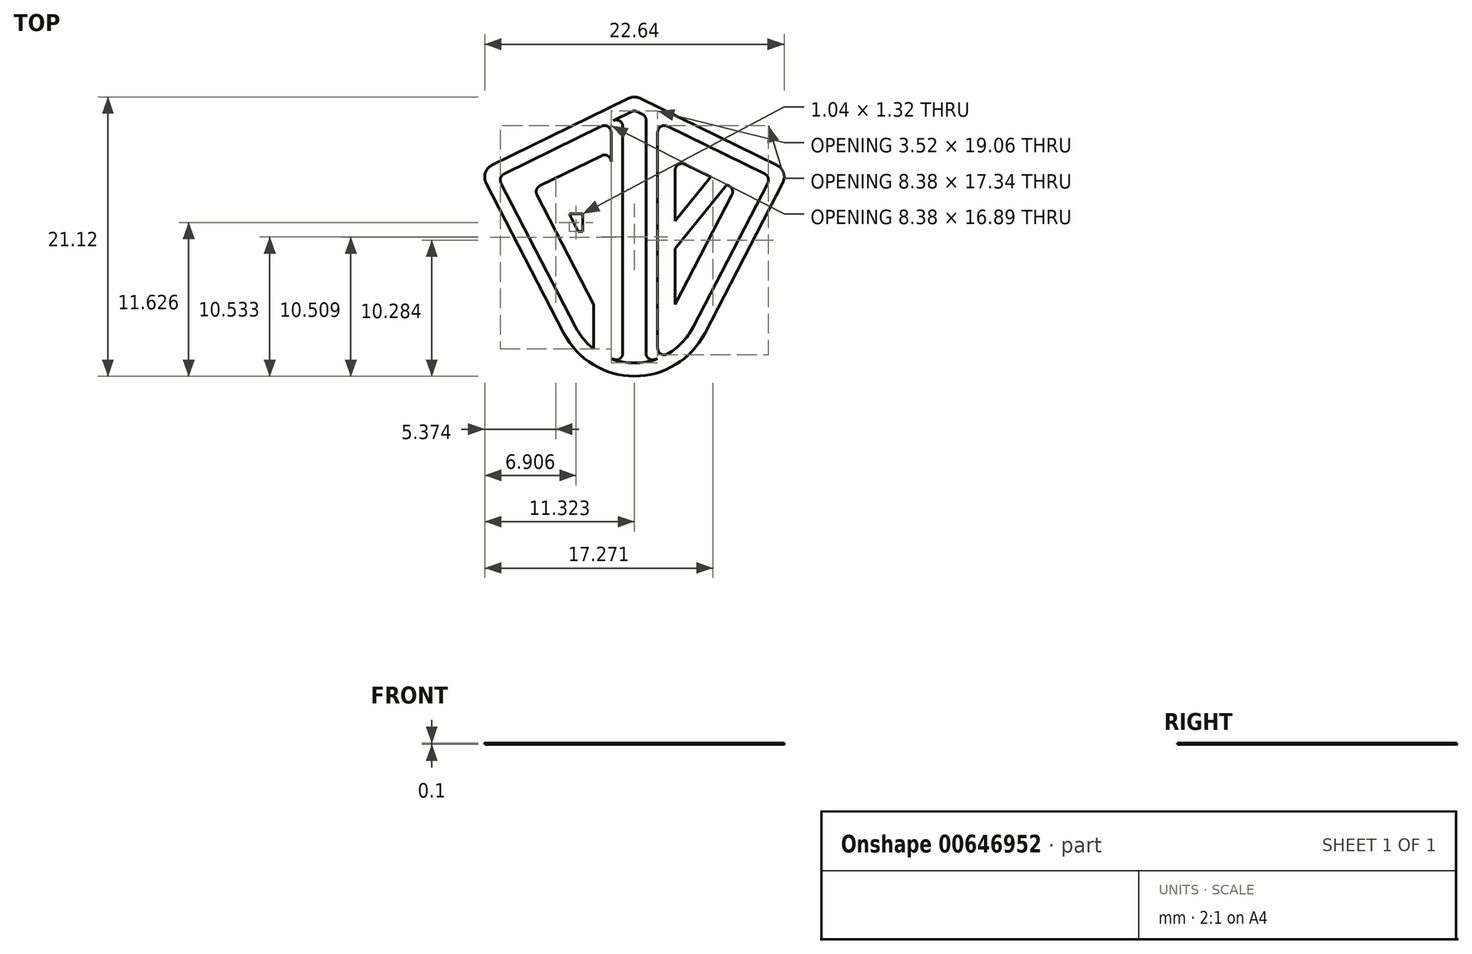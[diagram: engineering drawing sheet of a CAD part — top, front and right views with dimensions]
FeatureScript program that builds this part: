
annotation { "Feature Type Name" : "Feature", "Feature Type Description" : "" }
export const myFeature = defineFeature(function(context is Context, id is Id, definition is map)
    precondition{}
    {
        {
            var Q0;
            Q0=qCreatedBy(makeId("Top.planeOp"),FACE);
            var sketch = newSketch(context, id + "F0", { "sketchPlane" : qUnion([Q0])});
            skArc(sketch, "E0.MirrorCS", {"start": v(-12.62, 8.93) * mm, "mid": v(-12.18, 9.03) * mm, "end": v(-11.74, 8.93) * mm});
            skArc(sketch, "E1.MirrorCS", {"start": v(-1.42, 3.88) * mm, "mid": v(-0.9, 3.3) * mm, "end": v(-0.97, 2.52) * mm});
            skArc(sketch, "E2.MirrorCS", {"start": v(-23.38, 2.52) * mm, "mid": v(-23.45, 3.3) * mm, "end": v(-22.94, 3.88) * mm});
            skPoint(sketch, "E3.MirrorP", {"position": v(-23.85, 3.43) * mm});
            skArc(sketch, "E4.MirrorCS", {"start": v(-6.85, -8.84) * mm, "mid": v(-12.18, -12.09) * mm, "end": v(-17.5, -8.84) * mm});
            skLineSegment(sketch, "E5.MirrorCS", {"start": v(-6.85, -8.84) * mm, "end": v(-0.97, 2.52) * mm});
            skLineSegment(sketch, "E6.MirrorCS", {"start": v(-12.62, 8.93) * mm, "end": v(-22.94, 3.88) * mm});
            skLineSegment(sketch, "E7.MirrorCS", {"start": v(-23.38, 2.52) * mm, "end": v(-17.5, -8.84) * mm});
            skLineSegment(sketch, "E8.MirrorCS", {"start": v(-1.42, 3.88) * mm, "end": v(-11.74, 8.93) * mm});
            skLineSegment(sketch, "E9", {"start": v(-22.26, 2.53) * mm, "end": v(-16.62, -8.38) * mm});
            skArc(sketch, "E10.filletArc", {"start": v(-9.67, -10.41) * mm, "mid": v(-8.56, -9.53) * mm, "end": v(-7.74, -8.38) * mm});
            skLineSegment(sketch, "E11.MirrorCS", {"start": v(-10.42, 6.37) * mm, "end": v(-10.42, -9.98) * mm});
            skLineSegment(sketch, "E12.bottom", {"start": v(-15.25, 0.2) * mm, "end": v(-16.07, 0.2) * mm});
            skLineSegment(sketch, "E12.top", {"start": v(-15.75, -1.12) * mm, "end": v(-16.07, -1.12) * mm});
            skLineSegment(sketch, "E13", {"start": v(-15.25, 0.2) * mm, "end": v(-14.44, 0.2) * mm});
            skPoint(sketch, "E14", {"position": v(-16.57, -8.47) * mm});
            skPoint(sketch, "E15", {"position": v(-15.25, -10.03) * mm});
            skPoint(sketch, "E16", {"position": v(-13.94, -10.77) * mm});
            skPoint(sketch, "E17", {"position": v(-13.06, -11) * mm});
            skPoint(sketch, "E18", {"position": v(-11.3, -11) * mm});
            skPoint(sketch, "E19", {"position": v(-10.42, -10.77) * mm});
            skPoint(sketch, "E20", {"position": v(-9.1, -10.03) * mm});
            skPoint(sketch, "E21", {"position": v(-9.1, -6.67) * mm});
            skPoint(sketch, "E22", {"position": v(-2.78, 1.2) * mm});
            skPoint(sketch, "E23", {"position": v(-4.57, 2.08) * mm});
            skPoint(sketch, "E24", {"position": v(-9.1, 4.3) * mm});
            skPoint(sketch, "E25", {"position": v(-9.1, 6.52) * mm});
            skPoint(sketch, "E26", {"position": v(-10.42, 7.17) * mm});
            skPoint(sketch, "E27", {"position": v(-11.3, 7.6) * mm});
            skPoint(sketch, "E28", {"position": v(-13.06, 7.6) * mm});
            skPoint(sketch, "E29", {"position": v(-13.94, 7.17) * mm});
            skPoint(sketch, "E30", {"position": v(-15.25, 4.3) * mm});
            skPoint(sketch, "E31", {"position": v(-13.94, 4.94) * mm});
            skPoint(sketch, "E32", {"position": v(-13.06, 5.37) * mm});
            skPoint(sketch, "E33", {"position": v(-10.42, 4.94) * mm});
            skPoint(sketch, "E34", {"position": v(-11.3, 5.37) * mm});
            skPoint(sketch, "E35", {"position": v(-21.58, 1.2) * mm});
            skPoint(sketch, "E36", {"position": v(-19.78, 2.08) * mm});
            skPoint(sketch, "E37", {"position": v(-16.57, -4.12) * mm});
            skPoint(sketch, "E38", {"position": v(-16.57, -1.12) * mm});
            skPoint(sketch, "E39", {"position": v(-16.57, 0.2) * mm});
            skPoint(sketch, "E40", {"position": v(-15.25, 0.2) * mm});
            skPoint(sketch, "E41", {"position": v(-15.25, -1.12) * mm});
            skPoint(sketch, "E42", {"position": v(-13.94, 0.2) * mm});
            skLineSegment(sketch, "E43", {"start": v(-7.74, -8.38) * mm, "end": v(-2.78, 1.2) * mm});
            skLineSegment(sketch, "E44", {"start": v(-2.78, 1.2) * mm, "end": v(-2.1, 2.53) * mm});
            skLineSegment(sketch, "E45", {"start": v(-2.32, 3.2) * mm, "end": v(-9.1, 6.52) * mm});
            skLineSegment(sketch, "E46", {"start": v(-9.1, -6.67) * mm, "end": v(-4.8, 1.63) * mm});
            skLineSegment(sketch, "E47", {"start": v(-5.03, 2.3) * mm, "end": v(-8.38, 3.94) * mm});
            skLineSegment(sketch, "E48", {"start": v(-9.1, 3.5) * mm, "end": v(-9.1, -6.67) * mm});
            skLineSegment(sketch, "E49", {"start": v(-22.04, 3.2) * mm, "end": v(-14.65, 6.82) * mm});
            skLineSegment(sketch, "E50", {"start": v(-12.78, 7.74) * mm, "end": v(-12.4, 7.92) * mm});
            skLineSegment(sketch, "E51", {"start": v(-11.96, 7.92) * mm, "end": v(-11.58, 7.74) * mm});
            skLineSegment(sketch, "E52", {"start": v(-15.25, 4.3) * mm, "end": v(-19.32, 2.3) * mm});
            skLineSegment(sketch, "E53", {"start": v(-19.55, 1.63) * mm, "end": v(-16.57, -4.12) * mm});
            skLineSegment(sketch, "E54", {"start": v(-15.25, -1.62) * mm, "end": v(-15.25, -10.03) * mm});
            skPoint(sketch, "E55", {"position": v(-15.25, -6.67) * mm});
            skLineSegment(sketch, "E56", {"start": v(-16.57, -4.12) * mm, "end": v(-15.25, -6.67) * mm});
            skLineSegment(sketch, "E57", {"start": v(-15.25, 4.3) * mm, "end": v(-14.65, 4.59) * mm});
            skLineSegment(sketch, "E58", {"start": v(-9.1, 6.52) * mm, "end": v(-9.7, 6.82) * mm});
            skArc(sketch, "E59.filletArc", {"start": v(-22.04, 3.2) * mm, "mid": v(-22.3, 2.91) * mm, "end": v(-22.26, 2.53) * mm});
            skArc(sketch, "E60.filletArc", {"start": v(-2.1, 2.53) * mm, "mid": v(-2.06, 2.91) * mm, "end": v(-2.32, 3.2) * mm});
            skArc(sketch, "E61.filletArc", {"start": v(-13.94, 6.37) * mm, "mid": v(-14.17, 6.8) * mm, "end": v(-14.65, 6.82) * mm});
            skArc(sketch, "E62.filletArc", {"start": v(-9.7, 6.82) * mm, "mid": v(-10.18, 6.8) * mm, "end": v(-10.42, 6.37) * mm});
            skArc(sketch, "E63.filletArc", {"start": v(-8.38, 3.94) * mm, "mid": v(-8.87, 3.92) * mm, "end": v(-9.1, 3.5) * mm});
            skArc(sketch, "E64.filletArc", {"start": v(-4.8, 1.63) * mm, "mid": v(-4.78, 2.01) * mm, "end": v(-5.03, 2.3) * mm});
            skArc(sketch, "E65.filletArc", {"start": v(-19.32, 2.3) * mm, "mid": v(-19.58, 2.01) * mm, "end": v(-19.55, 1.63) * mm});
            skArc(sketch, "E66.filletArc", {"start": v(-13.94, 4.14) * mm, "mid": v(-14.17, 4.56) * mm, "end": v(-14.65, 4.59) * mm});
            skArc(sketch, "E67.filletArc", {"start": v(-15.25, -1.62) * mm, "mid": v(-15.4, -1.27) * mm, "end": v(-15.75, -1.12) * mm});
            skArc(sketch, "E68.filletArc", {"start": v(-13.94, -0.3) * mm, "mid": v(-14.08, 0.05) * mm, "end": v(-14.44, 0.2) * mm});
            skLineSegment(sketch, "E69", {"start": v(-13.94, 4.14) * mm, "end": v(-13.94, 6.37) * mm});
            skArc(sketch, "E70.filletArc", {"start": v(-11.96, 7.92) * mm, "mid": v(-12.18, 7.97) * mm, "end": v(-12.4, 7.92) * mm});
            skArc(sketch, "E71.filletArc", {"start": v(-12.78, 7.74) * mm, "mid": v(-12.98, 7.55) * mm, "end": v(-13.06, 7.29) * mm});
            skArc(sketch, "E72.filletArc", {"start": v(-11.3, 7.29) * mm, "mid": v(-11.37, 7.55) * mm, "end": v(-11.58, 7.74) * mm});
            skArc(sketch, "E73.filletArc", {"start": v(-10.42, -9.98) * mm, "mid": v(-10.17, -10.41) * mm, "end": v(-9.67, -10.41) * mm});
            skArc(sketch, "E74.MirrorCS", {"start": v(-14.69, -10.41) * mm, "mid": v(-15.8, -9.53) * mm, "end": v(-16.62, -8.38) * mm});
            skArc(sketch, "E75.MirrorCS", {"start": v(-13.94, -9.98) * mm, "mid": v(-14.19, -10.41) * mm, "end": v(-14.69, -10.41) * mm});
            skArc(sketch, "E76", {"start": v(-12.63, -11.1) * mm, "mid": v(-12.18, -11.14) * mm, "end": v(-11.72, -11.1) * mm});
            skLineSegment(sketch, "E77", {"start": v(-13.94, -9.98) * mm, "end": v(-13.94, -0.3) * mm});
            skLineSegment(sketch, "E78", {"start": v(-13.06, -10.61) * mm, "end": v(-13.06, 7.29) * mm});
            skLineSegment(sketch, "E79", {"start": v(-11.3, 7.29) * mm, "end": v(-11.3, -10.61) * mm});
            skArc(sketch, "E80.filletArc", {"start": v(-13.06, -10.61) * mm, "mid": v(-12.94, -10.94) * mm, "end": v(-12.63, -11.1) * mm});
            skArc(sketch, "E81.filletArc", {"start": v(-11.72, -11.1) * mm, "mid": v(-11.42, -10.94) * mm, "end": v(-11.3, -10.61) * mm});
            skPoint(sketch, "E82", {"position": v(-17.53, 0.99) * mm});
            skLineSegment(sketch, "E83", {"start": v(-16.07, 0.2) * mm, "end": v(-17.12, 0.2) * mm});
            skLineSegment(sketch, "E84", {"start": v(-16.07, -1.12) * mm, "end": v(-16.57, -1.12) * mm});
            skPoint(sketch, "E85", {"position": v(-16.43, -1.12) * mm});
            skLineSegment(sketch, "E86", {"start": v(-16.43, -1.12) * mm, "end": v(-17.12, 0.2) * mm});
            skLineSegment(sketch, "E87", {"start": v(-13.94, 7.17) * mm, "end": v(-13.78, 7.25) * mm});
            skLineSegment(sketch, "E88", {"start": v(-13.06, 5.37) * mm, "end": v(-13.06, 6.8) * mm});
            skArc(sketch, "E89.filletArc", {"start": v(-13.06, 6.8) * mm, "mid": v(-13.3, 7.22) * mm, "end": v(-13.78, 7.25) * mm});
            skLineSegment(sketch, "E90", {"start": v(-13.94, 7.17) * mm, "end": v(-12.78, 7.74) * mm});
            skLineSegment(sketch, "E91", {"start": v(-13.94, -10.77) * mm, "end": v(-13.69, -10.83) * mm});
            skLineSegment(sketch, "E92", {"start": v(-13.06, 5.37) * mm, "end": v(-13.06, -10.35) * mm});
            skArc(sketch, "E93.filletArc", {"start": v(-13.69, -10.83) * mm, "mid": v(-13.25, -10.75) * mm, "end": v(-13.06, -10.35) * mm});
            skLineSegment(sketch, "E94", {"start": v(-21.58, 1.2) * mm, "end": v(-16.62, -8.38) * mm});
            skLineSegment(sketch, "E95", {"start": v(-2.78, 1.2) * mm, "end": v(-7.74, -8.38) * mm});
            skArc(sketch, "E96.filletArc", {"start": v(-16.62, -8.38) * mm, "mid": v(-12.18, -11.09) * mm, "end": v(-7.74, -8.38) * mm});
            skLineSegment(sketch, "E97", {"start": v(-12.18, -8.2) * mm, "end": v(-12.18, -5.08) * mm});
            skArc(sketch, "E98.MirrorCS", {"start": v(-10.67, -10.83) * mm, "mid": v(-11.1, -10.75) * mm, "end": v(-11.3, -10.35) * mm});
            skLineSegment(sketch, "E99.MirrorCS", {"start": v(-10.42, -10.77) * mm, "end": v(-10.67, -10.83) * mm});
            skPoint(sketch, "E100", {"position": v(-9.1, -0.13) * mm});
            skPoint(sketch, "E101", {"position": v(-5.14, 2.36) * mm});
            skPoint(sketch, "E102", {"position": v(-4.77, 1.99) * mm});
            skPoint(sketch, "E103", {"position": v(-4.96, 1.34) * mm});
            skPoint(sketch, "E104", {"position": v(-9.1, -0.69) * mm});
            skPoint(sketch, "E105", {"position": v(-9.1, 0.42) * mm});
            skLineSegment(sketch, "E106", {"start": v(-16.07, -1.12) * mm, "end": v(-16.07, 0.2) * mm});
            skPoint(sketch, "E107", {"position": v(-5.47, 2.52) * mm});
            skPoint(sketch, "E108", {"position": v(-5.95, 2.75) * mm});
            skLineSegment(sketch, "E109", {"start": v(-6.06, 2.8) * mm, "end": v(-5.2, 2.39) * mm});
            skLineSegment(sketch, "E110", {"start": v(-5.2, 2.39) * mm, "end": v(-5.23, 2.36) * mm});
            skPoint(sketch, "E111", {"position": v(-9.1, 0.2) * mm});
            skPoint(sketch, "E112", {"position": v(-9.1, -1.12) * mm});
            skLineSegment(sketch, "E113", {"start": v(-9.1, -2.44) * mm, "end": v(-5.2, 2.39) * mm});
            skLineSegment(sketch, "E114", {"start": v(-7.8, 1.26) * mm, "end": v(-6.26, 3.17) * mm});
            skLineSegment(sketch, "E115", {"start": v(-7.8, 1.26) * mm, "end": v(-9.23, -0.5) * mm});
            skSolve(sketch);
        }
        {
            var Q0;
            {var subQ0=sQuery(id+"F0.wireOp",EDGE,"E46");Q0=makeQuery(id+"F0.imprint","IMPRINT",FACE,{"disambiguationData":[TD([[makeQuery(id+"F0.imprint","IMPRINT",EDGE,{"derivedFrom":subQ0}),1.0]])]});}
            var Q1;
            {var subQ0=sQuery(id+"F0.wireOp",EDGE,"E63.filletArc");Q1=makeQuery(id+"F0.imprint","IMPRINT",FACE,{"disambiguationData":[TD([[makeQuery(id+"F0.imprint","IMPRINT",EDGE,{"derivedFrom":subQ0}),1.0]])]});}
            var Q2;
            Q2=makeQuery(id+"F0.imprint","IMPRINT",FACE,{"disambiguationData":[TD([[makeQuery(id+"F0.imprint","IMPRINT",EDGE,{"derivedFrom":sQuery(id+"F0.wireOp",EDGE,"E0.MirrorCS")}),-1.0]])]});
            var Q3;
            {var subQ0=sQuery(id+"F0.wireOp",EDGE,"E76");Q3=makeQuery(id+"F0.imprint","IMPRINT",FACE,{"disambiguationData":[TD([[makeQuery(id+"F0.imprint","IMPRINT",EDGE,{"derivedFrom":subQ0}),1.0]])]});}
            var Q4;
            {var subQ3=sQuery(id+"F0.wireOp",EDGE,"RPIov1bO-qwDe-22lU-BV6p-ET71WXEMnufC");Q4=makeQuery(id+"F0.imprint","IMPRINT",FACE,{"disambiguationData":[TD([[makeQuery(id+"F0.imprint","IMPRINT",EDGE,{"derivedFrom":subQ3}),-1.0]])]});}
            var Q5;
            {var subQ5=sQuery(id+"F0.wireOp",EDGE,"E75.MirrorCS");Q5=makeQuery(id+"F0.imprint","IMPRINT",FACE,{"disambiguationData":[TD([[makeQuery(id+"F0.imprint","IMPRINT",EDGE,{"derivedFrom":subQ5}),1.0]])]});}
            var Q6;
            {var subQ1=sQuery(id+"F0.wireOp",EDGE,"E68.filletArc");Q6=makeQuery(id+"F0.imprint","IMPRINT",FACE,{"disambiguationData":[TD([[makeQuery(id+"F0.imprint","IMPRINT",EDGE,{"derivedFrom":subQ1}),-1.0]])]});}
            var Q7;
            {var subQ1=sQuery(id+"F0.wireOp",EDGE,"E73.filletArc");Q7=makeQuery(id+"F0.imprint","IMPRINT",FACE,{"disambiguationData":[TD([[makeQuery(id+"F0.imprint","IMPRINT",EDGE,{"derivedFrom":subQ1}),-1.0]])]});}
            var Q8;
            {var subQ0=sQuery(id+"F0.wireOp",EDGE,"Cl3IQgta-nqtW-K0ye-efcI-YpJCdKnWrlVx");var subQ1=sQuery(id+"F0.wireOp",EDGE,"E11.MirrorCS");var subQ2=makeQuery(id+"F0.imprint","INTERSECT",VERTEX,{"derivedFrom":[subQ1,subQ0]});Q8=makeQuery(id+"F0.imprint","IMPRINT",FACE,{"disambiguationData":[TD([[makeQuery(id+"F0.imprint","IMPRINT",EDGE,{"disambiguationData":[TD([[subQ2,-1.0]])],"derivedFrom":subQ1}),-1.0]])]});}
            var Q9;
            {var subQ0=sQuery(id+"F0.wireOp",EDGE,"E48");var subQ1=sQuery(id+"F0.wireOp",EDGE,"E46");var subQ2=makeQuery(id+"F0.imprint","INTERSECT",VERTEX,{"derivedFrom":[subQ1,subQ0]});Q9=makeQuery(id+"F0.imprint","IMPRINT",FACE,{"disambiguationData":[TD([[makeQuery(id+"F0.imprint","IMPRINT",EDGE,{"disambiguationData":[TD([[subQ2,-1.0]])],"derivedFrom":subQ1}),1.0]])]});}
            var Q10;
            {var subQ0=sQuery(id+"F0.wireOp",EDGE,"tmzpQr5O-wWc1-ln0N-NPHb-jfIugI6lGER6");var subQ1=sQuery(id+"F0.wireOp",EDGE,"w3vRnku4-Teg6-SXiI-nqO1-kFEqONE9hBVN");var subQ2=makeQuery(id+"F0.imprint","INTERSECT",VERTEX,{"derivedFrom":[subQ1,subQ0]});Q10=makeQuery(id+"F0.imprint","IMPRINT",FACE,{"disambiguationData":[TD([[makeQuery(id+"F0.imprint","IMPRINT",EDGE,{"disambiguationData":[TD([[subQ2,-1.0]])],"derivedFrom":subQ1}),1.0]])]});}
            var Q11;
            {var subQ1=sQuery(id+"F0.wireOp",EDGE,"E46");var subQ5=sQuery(id+"F0.wireOp",EDGE,"Cl3IQgta-nqtW-K0ye-efcI-YpJCdKnWrlVx");var subQ6=makeQuery(id+"F0.imprint","INTERSECT",VERTEX,{"derivedFrom":[subQ1,subQ5]});Q11=makeQuery(id+"F0.imprint","IMPRINT",FACE,{"disambiguationData":[TD([[makeQuery(id+"F0.imprint","IMPRINT",EDGE,{"disambiguationData":[TD([[subQ6,1.0]])],"derivedFrom":subQ1}),1.0]])]});}
            var Q12;
            {var subQ0=sQuery(id+"F0.wireOp",EDGE,"E110");Q12=makeQuery(id+"F0.imprint","IMPRINT",FACE,{"disambiguationData":[TD([[makeQuery(id+"F0.imprint","IMPRINT",EDGE,{"derivedFrom":subQ0}),1.0]])]});}
            var Q13;
            {var subQ0=sQuery(id+"F0.wireOp",EDGE,"tmzpQr5O-wWc1-ln0N-NPHb-jfIugI6lGER6");var subQ1=sQuery(id+"F0.wireOp",EDGE,"E11.MirrorCS");var subQ2=makeQuery(id+"F0.imprint","INTERSECT",VERTEX,{"derivedFrom":[subQ1,subQ0]});Q13=makeQuery(id+"F0.imprint","IMPRINT",FACE,{"disambiguationData":[TD([[makeQuery(id+"F0.imprint","IMPRINT",EDGE,{"disambiguationData":[TD([[subQ2,-1.0]])],"derivedFrom":subQ1}),-1.0]])]});}
            var Q14;
            {var subQ0=sQuery(id+"F0.wireOp",EDGE,"afa05864-eb28-49e8-95be-b6718b75a2b20.MirrorCS");var subQ1=sQuery(id+"F0.wireOp",EDGE,"E77");var subQ2=makeQuery(id+"F0.imprint","INTERSECT",VERTEX,{"derivedFrom":[subQ1,subQ0]});Q14=makeQuery(id+"F0.imprint","IMPRINT",FACE,{"disambiguationData":[TD([[makeQuery(id+"F0.imprint","IMPRINT",EDGE,{"disambiguationData":[TD([[subQ2,-1.0]])],"derivedFrom":subQ1}),-1.0]])]});}
            var Q15;
            {var subQ5=sQuery(id+"F0.wireOp",EDGE,"E47");var subQ7=sQuery(id+"F0.wireOp",EDGE,"a02aedb6-8c73-418c-b080-1dd0916ab2010.MirrorCS");var subQ9=makeQuery(id+"F0.imprint","INTERSECT",VERTEX,{"derivedFrom":[subQ5,subQ7]});Q15=makeQuery(id+"F0.imprint","IMPRINT",FACE,{"disambiguationData":[TD([[makeQuery(id+"F0.imprint","IMPRINT",EDGE,{"disambiguationData":[TD([[subQ9,1.0]])],"derivedFrom":subQ7}),-1.0]])]});}
            var Q16;
            {var subQ0=sQuery(id+"F0.wireOp",EDGE,"afa05864-eb28-49e8-95be-b6718b75a2b20.MirrorCS");var subQ1=sQuery(id+"F0.wireOp",EDGE,"w3vRnku4-Teg6-SXiI-nqO1-kFEqONE9hBVN");var subQ2=makeQuery(id+"F0.imprint","INTERSECT",VERTEX,{"derivedFrom":[subQ1,subQ0]});Q16=makeQuery(id+"F0.imprint","IMPRINT",FACE,{"disambiguationData":[TD([[makeQuery(id+"F0.imprint","IMPRINT",EDGE,{"disambiguationData":[TD([[subQ2,-1.0]])],"derivedFrom":subQ1}),1.0]])]});}
            var Q17;
            {var subQ5=sQuery(id+"F0.wireOp",EDGE,"E64.filletArc");var subQ6=sQuery(id+"F0.wireOp",EDGE,"E46");var subQ7=makeQuery(id+"F0.imprint","INTERSECT",VERTEX,{"derivedFrom":[subQ6,subQ5]});Q17=makeQuery(id+"F0.imprint","IMPRINT",FACE,{"disambiguationData":[TD([[makeQuery(id+"F0.imprint","IMPRINT",EDGE,{"disambiguationData":[TD([[subQ7,1.0]])],"derivedFrom":subQ6}),1.0]])]});}
            var Q18;
            {var subQ1=sQuery(id+"F0.wireOp",EDGE,"E64.filletArc");var subQ7=sQuery(id+"F0.wireOp",EDGE,"E47");var subQ8=makeQuery(id+"F0.imprint","INTERSECT",VERTEX,{"derivedFrom":[subQ7,subQ1]});Q18=makeQuery(id+"F0.imprint","IMPRINT",FACE,{"disambiguationData":[TD([[makeQuery(id+"F0.imprint","IMPRINT",EDGE,{"disambiguationData":[TD([[subQ8,1.0]])],"derivedFrom":subQ1}),1.0]])]});}
            var Q19;
            {var subQ0=sQuery(id+"F0.wireOp",EDGE,"SzZBVxO3-oEJs-8OU1-3VI5-5WsEBxKBmkIE");var subQ1=sQuery(id+"F0.wireOp",EDGE,"w3vRnku4-Teg6-SXiI-nqO1-kFEqONE9hBVN");var subQ2=makeQuery(id+"F0.imprint","INTERSECT",VERTEX,{"derivedFrom":[subQ1,subQ0]});Q19=makeQuery(id+"F0.imprint","IMPRINT",FACE,{"disambiguationData":[TD([[makeQuery(id+"F0.imprint","IMPRINT",EDGE,{"disambiguationData":[TD([[subQ2,-1.0]])],"derivedFrom":subQ1}),1.0]])]});}
            var Q20;
            {var subQ0=sQuery(id+"F0.wireOp",EDGE,"Cl3IQgta-nqtW-K0ye-efcI-YpJCdKnWrlVx");var subQ1=sQuery(id+"F0.wireOp",EDGE,"w3vRnku4-Teg6-SXiI-nqO1-kFEqONE9hBVN");var subQ2=makeQuery(id+"F0.imprint","INTERSECT",VERTEX,{"derivedFrom":[subQ1,subQ0]});Q20=makeQuery(id+"F0.imprint","IMPRINT",FACE,{"disambiguationData":[TD([[makeQuery(id+"F0.imprint","IMPRINT",EDGE,{"disambiguationData":[TD([[subQ2,-1.0]])],"derivedFrom":subQ1}),1.0]])]});}
            var Q21;
            {var subQ0=sQuery(id+"F0.wireOp",EDGE,"SzZBVxO3-oEJs-8OU1-3VI5-5WsEBxKBmkIE");var subQ1=sQuery(id+"F0.wireOp",EDGE,"w3vRnku4-Teg6-SXiI-nqO1-kFEqONE9hBVN");var subQ2=makeQuery(id+"F0.imprint","INTERSECT",VERTEX,{"derivedFrom":[subQ1,subQ0]});Q21=makeQuery(id+"F0.imprint","IMPRINT",FACE,{"disambiguationData":[TD([[makeQuery(id+"F0.imprint","IMPRINT",EDGE,{"disambiguationData":[TD([[subQ2,-1.0]])],"derivedFrom":subQ1}),-1.0]])]});}
            var Q22;
            {var subQ0=sQuery(id+"F0.wireOp",EDGE,"afa05864-eb28-49e8-95be-b6718b75a2b20.MirrorCS");var subQ1=sQuery(id+"F0.wireOp",EDGE,"E46");var subQ2=makeQuery(id+"F0.imprint","INTERSECT",VERTEX,{"derivedFrom":[subQ1,subQ0]});Q22=makeQuery(id+"F0.imprint","IMPRINT",FACE,{"disambiguationData":[TD([[makeQuery(id+"F0.imprint","IMPRINT",EDGE,{"disambiguationData":[TD([[subQ2,-1.0]])],"derivedFrom":subQ1}),1.0]])]});}
            var Q23;
            {var subQ1=sQuery(id+"F0.wireOp",EDGE,"E109");Q23=makeQuery(id+"F0.imprint","IMPRINT",FACE,{"disambiguationData":[TD([[makeQuery(id+"F0.imprint","IMPRINT",EDGE,{"derivedFrom":subQ1}),-1.0]])]});}
            extrude(context, id + "F1", {"entities" : qUnion([Q0, Q1, Q2, Q3, Q4, Q5, Q6, Q7, Q8, Q9, Q10, Q11, Q12, Q13, Q14, Q15, Q16, Q17, Q18, Q19, Q20, Q21, Q22, Q23]), "depth" : .1 * mm, "offsetDistance" : 25 * mm});
        }
    });
